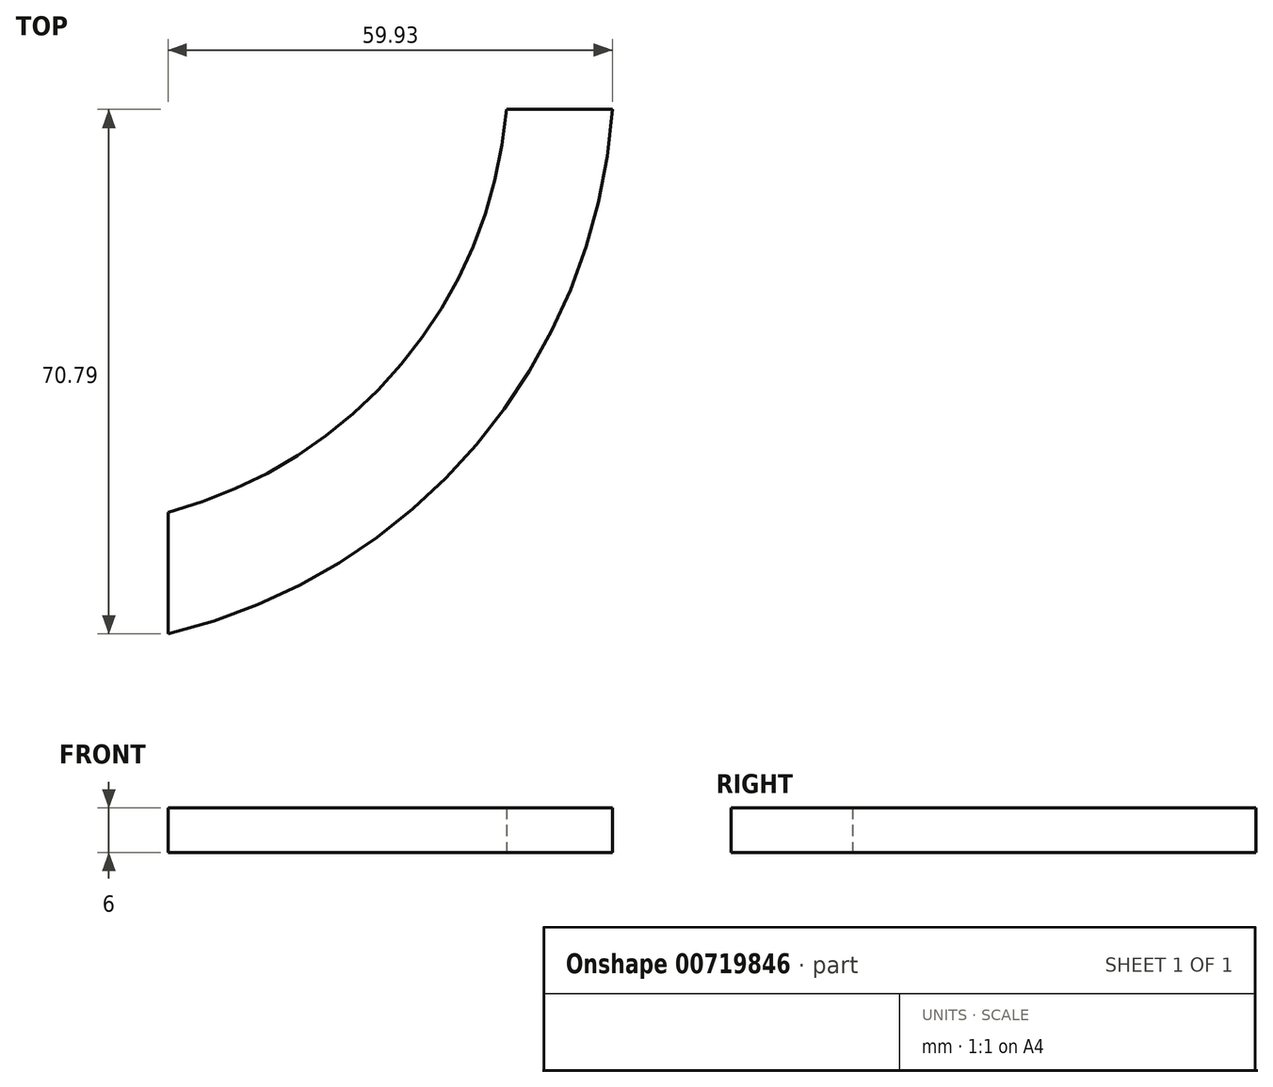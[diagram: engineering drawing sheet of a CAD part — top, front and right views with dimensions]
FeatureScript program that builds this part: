
annotation { "Feature Type Name" : "Feature", "Feature Type Description" : "" }
export const myFeature = defineFeature(function(context is Context, id is Id, definition is map)
    precondition{}
    {
        {
            var Q0;
            Q0=qCreatedBy(makeId("Top.planeOp"),FACE);
            var sketch = newSketch(context, id + "F0", { "sketchPlane" : qUnion([Q0])});
            skLineSegment(sketch, "E0", {"start": v(45.65, 49.1) * mm, "end": v(59.93, 49.1) * mm});
            skLineSegment(sketch, "E1", {"start": v(0, -5.29) * mm, "end": v(0, -21.7) * mm});
            skArc(sketch, "E2", {"start": v(0, -21.7) * mm, "mid": v(41.6, 3.85) * mm, "end": v(59.93, 49.1) * mm});
            skArc(sketch, "E3", {"start": v(0, -5.29) * mm, "mid": v(31.45, 14.66) * mm, "end": v(45.65, 49.1) * mm});
            skPoint(sketch, "E4.orphan", {"position": v(0, 49.1) * mm});
            skSolve(sketch);
        }
        {
            var Q0;
            Q0 = qSketchRegion(id + "F0", true);
            extrude(context, id + "F1", {"entities" : qUnion([Q0]), "depth" : 6 * mm, "offsetDistance" : 25 * mm});
        }
    });
